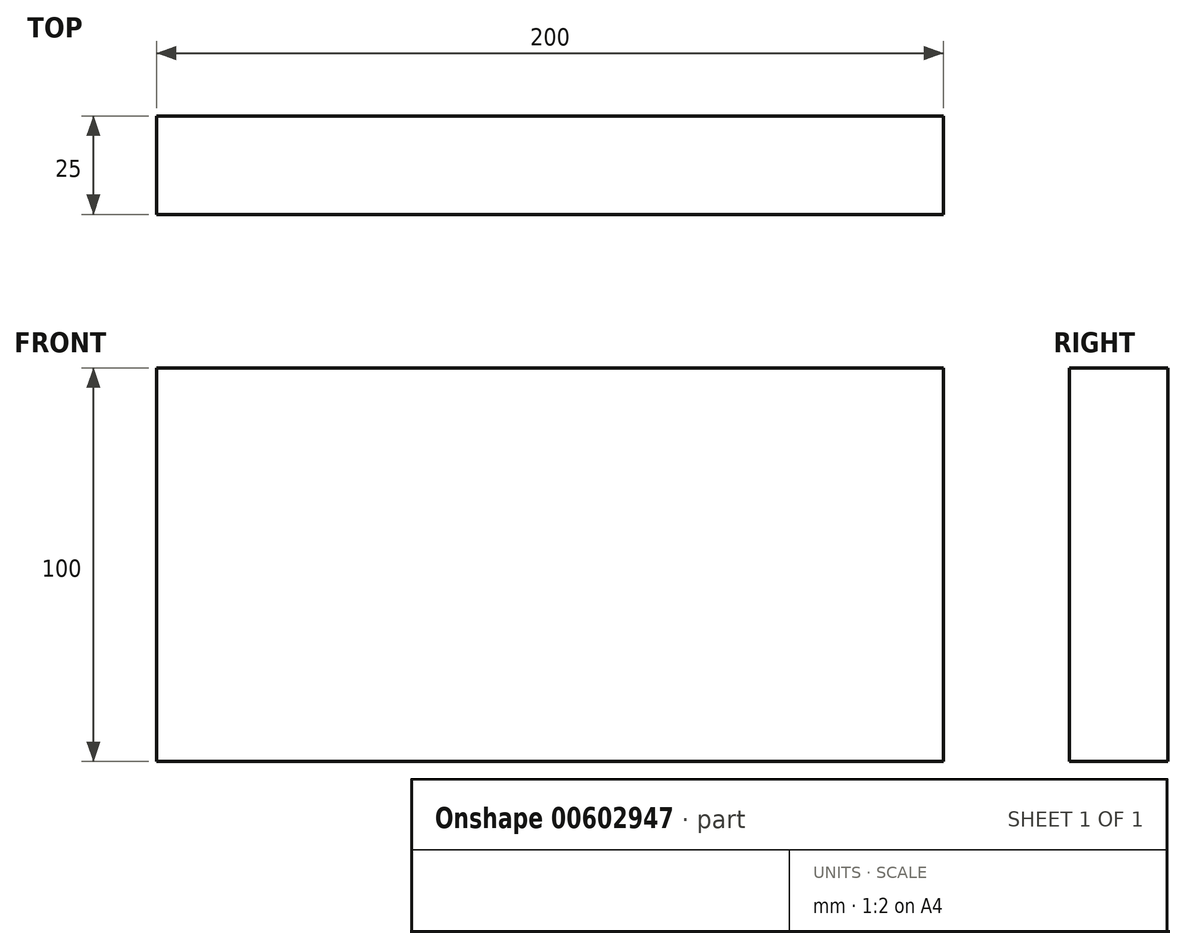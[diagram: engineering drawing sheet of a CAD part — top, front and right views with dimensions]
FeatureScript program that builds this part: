
annotation { "Feature Type Name" : "Feature", "Feature Type Description" : "" }
export const myFeature = defineFeature(function(context is Context, id is Id, definition is map)
    precondition{}
    {
        {
            var Q0;
            Q0=qCreatedBy(makeId("Front.planeOp"),FACE);
            var sketch = newSketch(context, id + "F0", { "sketchPlane" : qUnion([Q0])});
            skLineSegment(sketch, "E0.bottom", {"start": v(-100, 50) * mm, "end": v(100, 50) * mm});
            skLineSegment(sketch, "E0.top", {"start": v(-100, -50) * mm, "end": v(100, -50) * mm});
            skLineSegment(sketch, "E0.left", {"start": v(-100, 50) * mm, "end": v(-100, -50) * mm});
            skLineSegment(sketch, "E0.right", {"start": v(100, 50) * mm, "end": v(100, -50) * mm});
            skPoint(sketch, "E0.middle", {"position": v(0, 0) * mm});
            skSolve(sketch);
        }
        {
            var Q0;
            Q0=makeQuery(id+"F0.imprint","IMPRINT",FACE,{"disambiguationData":[TD([[makeQuery(id+"F0.imprint","IMPRINT",EDGE,{"derivedFrom":sQuery(id+"F0.wireOp",EDGE,"E0.bottom")}),-1.0]])]});
            extrude(context, id + "F1", {"entities" : qUnion([Q0]), "depth" : 25 * mm, "offsetDistance" : 25 * mm});
        }
    });
